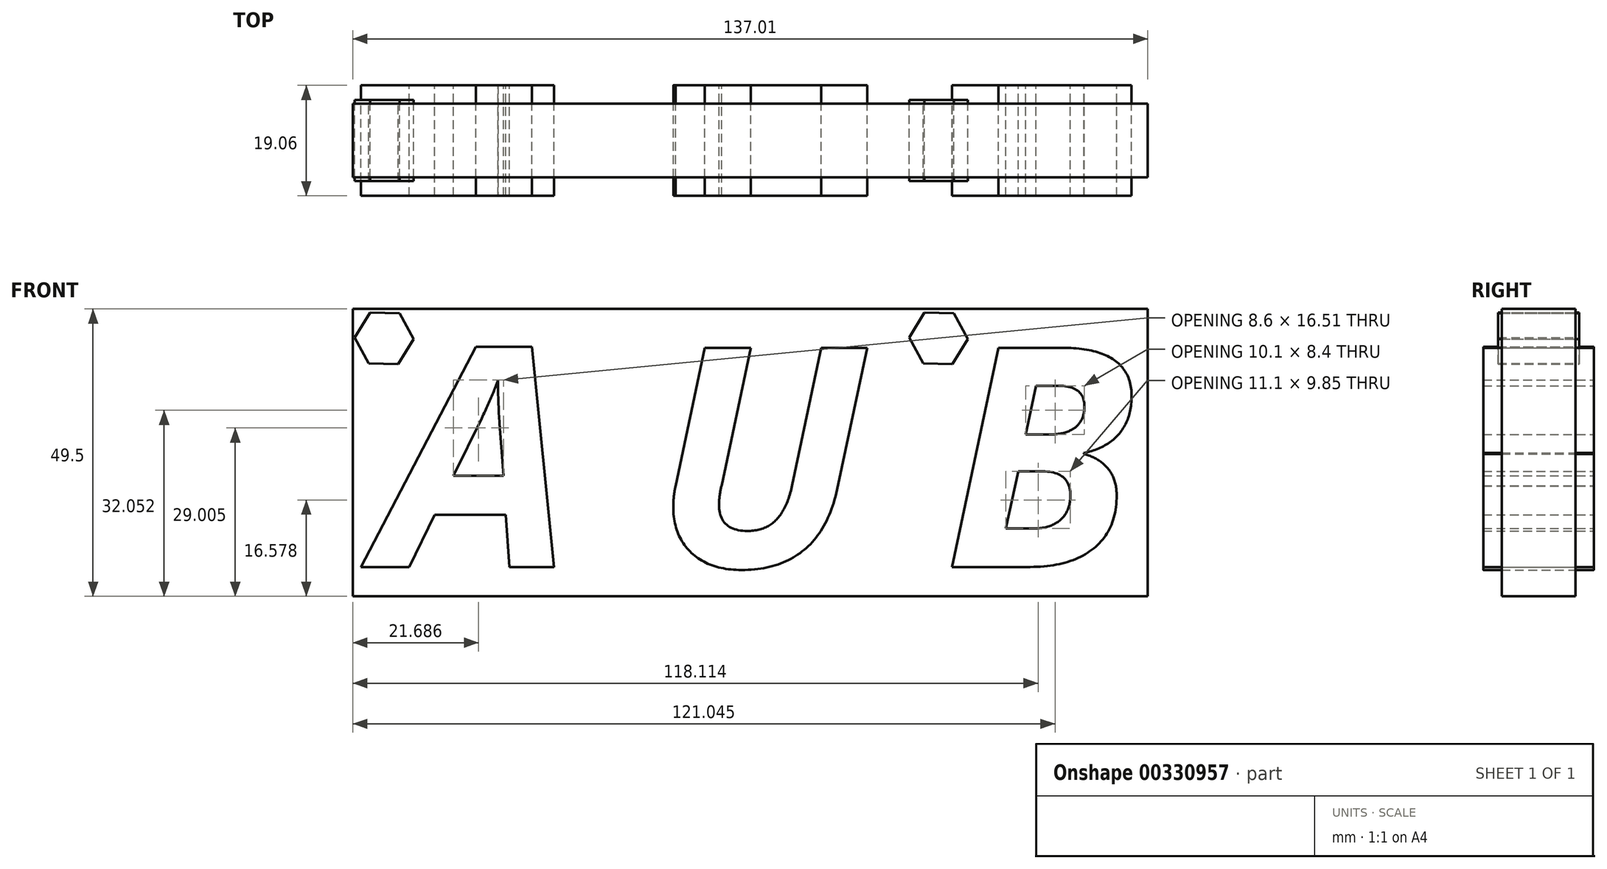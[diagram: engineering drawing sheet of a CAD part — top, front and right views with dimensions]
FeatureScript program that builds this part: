
annotation { "Feature Type Name" : "Feature", "Feature Type Description" : "" }
export const myFeature = defineFeature(function(context is Context, id is Id, definition is map)
    precondition{}
    {
        {
            var Q0;
            Q0=qCreatedBy(makeId("Front.planeOp"),FACE);
            var sketch = newSketch(context, id + "F0", { "sketchPlane" : qUnion([Q0])});
            skText(sketch, "E0", { "text": "A U B", "fontName": "OpenSans-BoldItalic.ttf"});
            const initialGuessF0  = {"E0": [-0.0676, -0.01884, 1, 0, 0.0381]};
            skSetInitialGuess(sketch, initialGuessF0);
            skSolve(sketch);
        }
        {
            var Q0;
            Q0=qSketchRegion(id+"F0",true);
            extrude(context, id + "F1", {"entities" : qUnion([Q0]), "endBound" : BoundingType.SYMMETRIC, "depth" : 19.05 * mm});
        }
        {
            var Q0;
            Q0=qCreatedBy(makeId("Front.planeOp"),FACE);
            var sketch = newSketch(context, id + "F2", { "sketchPlane" : qUnion([Q0])});
            skLineSegment(sketch, "E1.bottom", {"start": v(-72.22, 25.62) * mm, "end": v(64.8, 25.62) * mm});
            skLineSegment(sketch, "E1.top", {"start": v(-72.22, -23.88) * mm, "end": v(64.8, -23.88) * mm});
            skLineSegment(sketch, "E1.left", {"start": v(-72.22, 25.62) * mm, "end": v(-72.22, -23.88) * mm});
            skLineSegment(sketch, "E1.right", {"start": v(64.8, 25.62) * mm, "end": v(64.8, -23.88) * mm});
            skSolve(sketch);
        }
        {
            var Q0;
            Q0=makeQuery(id+"F2.imprint","IMPRINT",FACE,{"disambiguationData":[TD([[makeQuery(id+"F2.imprint","IMPRINT",EDGE,{"derivedFrom":sQuery(id+"F2.wireOp",EDGE,"E1.bottom")}),-1.0]])]});
            extrude(context, id + "F3", {"entities" : qUnion([Q0]), "endBound" : BoundingType.SYMMETRIC, "depth" : 12.7 * mm});
        }
        {
            var Q0;
            Q0=qCreatedBy(makeId("Front.planeOp"),FACE);
            var sketch = newSketch(context, id + "F4", { "sketchPlane" : qUnion([Q0])});
            skCircle(sketch, "E2.cCircle", {"center": v(-67.03, 20.55) * mm, "radius": 4.4 * mm, "construction": true});
            skLineSegment(sketch, "E2.0", {"start": v(-61.72, 20.41) * mm, "end": v(-64.38, 16.1) * mm});
            skLineSegment(sketch, "E2.1", {"start": v(-64.38, 16.1) * mm, "end": v(-69.45, 16.23) * mm});
            skLineSegment(sketch, "E2.2", {"start": v(-69.45, 16.23) * mm, "end": v(-71.86, 20.7) * mm});
            skLineSegment(sketch, "E2.3", {"start": v(-71.86, 20.7) * mm, "end": v(-69.2, 25.02) * mm});
            skLineSegment(sketch, "E2.4", {"start": v(-69.2, 25.02) * mm, "end": v(-64.13, 24.87) * mm});
            skLineSegment(sketch, "E2.5", {"start": v(-64.13, 24.87) * mm, "end": v(-61.72, 20.41) * mm});
            skPoint(sketch, "E2.0.midPoint", {"position": v(-67.03, 20.55) * mm});
            skLineSegment(sketch, "E3.0", {"start": v(33.8, 20.41) * mm, "end": v(31.15, 16.1) * mm});
            skLineSegment(sketch, "E3.1", {"start": v(31.15, 16.1) * mm, "end": v(26.08, 16.23) * mm});
            skLineSegment(sketch, "E3.2", {"start": v(26.08, 16.23) * mm, "end": v(23.66, 20.7) * mm});
            skLineSegment(sketch, "E3.3", {"start": v(23.66, 20.7) * mm, "end": v(26.32, 25.02) * mm});
            skLineSegment(sketch, "E3.4", {"start": v(26.32, 25.02) * mm, "end": v(31.4, 24.87) * mm});
            skLineSegment(sketch, "E3.5", {"start": v(31.4, 24.87) * mm, "end": v(33.8, 20.41) * mm});
            skSolve(sketch);
        }
        {
            var Q0;
            Q0 = qSketchRegion(id + "F4", true);
            extrude(context, id + "F5", {"entities" : qUnion([Q0]), "endBound" : BoundingType.SYMMETRIC, "depth" : 13.97 * mm});
        }
    });
